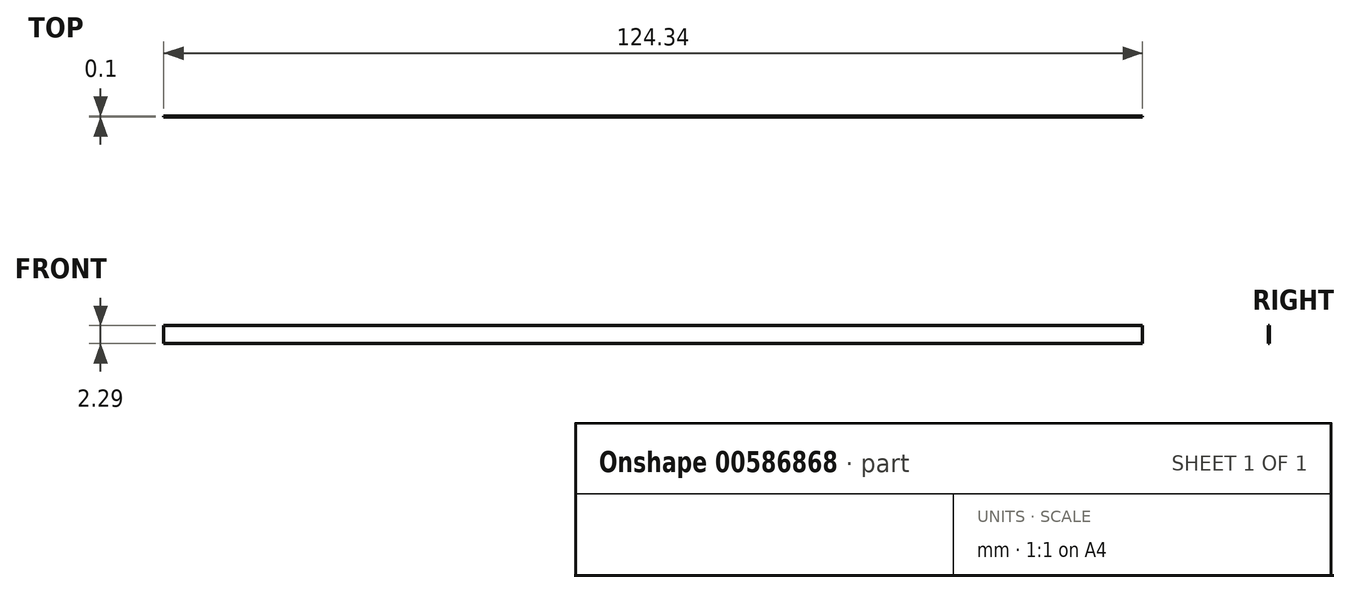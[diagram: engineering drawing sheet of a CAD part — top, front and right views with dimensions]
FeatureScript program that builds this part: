
annotation { "Feature Type Name" : "Feature", "Feature Type Description" : "" }
export const myFeature = defineFeature(function(context is Context, id is Id, definition is map)
    precondition{}
    {
        {
            var Q0;
            Q0=qCreatedBy(makeId("Front.planeOp"),FACE);
            var sketch = newSketch(context, id + "F0", { "sketchPlane" : qUnion([Q0])});
            skLineSegment(sketch, "E0.bottom", {"start": v(-52.92, -5.08) * mm, "end": v(71.42, -5.08) * mm});
            skLineSegment(sketch, "E0.top", {"start": v(-52.92, -7.37) * mm, "end": v(71.42, -7.37) * mm});
            skLineSegment(sketch, "E0.left", {"start": v(-52.92, -5.08) * mm, "end": v(-52.92, -7.37) * mm});
            skLineSegment(sketch, "E0.right", {"start": v(71.42, -5.08) * mm, "end": v(71.42, -7.37) * mm});
            skSolve(sketch);
        }
        {
            var Q0;
            Q0=makeQuery(id+"F0.imprint","IMPRINT",FACE,{"disambiguationData":[TD([[makeQuery(id+"F0.imprint","IMPRINT",EDGE,{"derivedFrom":sQuery(id+"F0.wireOp",EDGE,"E0.bottom")}),-1.0]])]});
            extrude(context, id + "F1", {"entities" : qUnion([Q0]), "depth" : 0.1 * mm, "offsetDistance" : 25 * mm});
        }
    });
